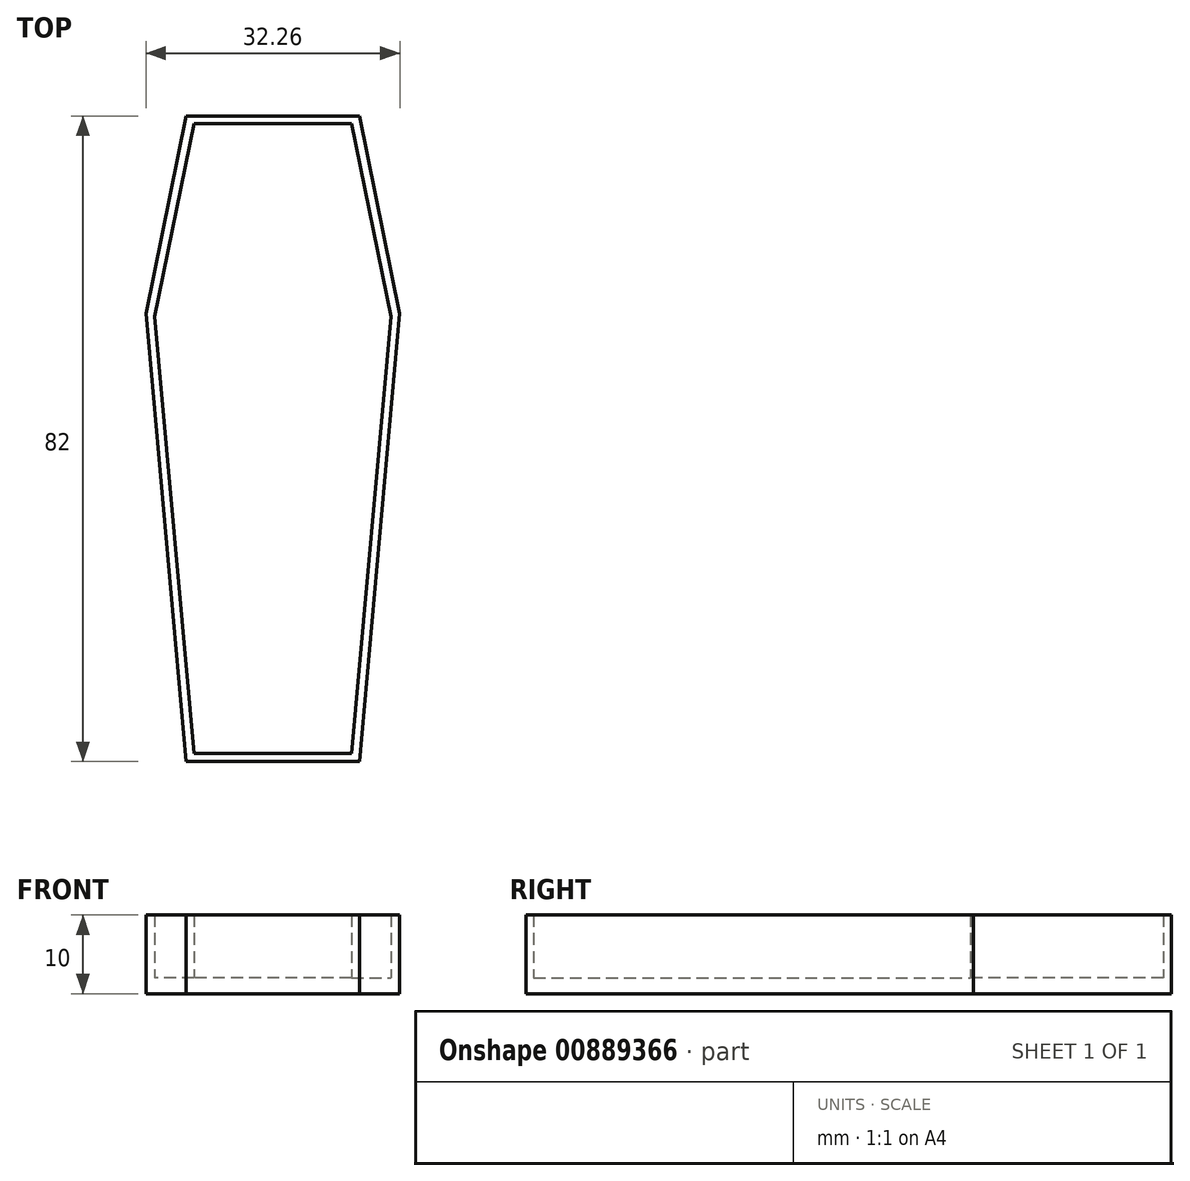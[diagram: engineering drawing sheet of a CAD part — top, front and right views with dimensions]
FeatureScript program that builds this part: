
annotation { "Feature Type Name" : "Feature", "Feature Type Description" : "" }
export const myFeature = defineFeature(function(context is Context, id is Id, definition is map)
    precondition{}
    {
        {
            var Q0;
            Q0=qCreatedBy(makeId("Top.planeOp"),FACE);
            var sketch = newSketch(context, id + "F0", { "sketchPlane" : qUnion([Q0])});
            skLineSegment(sketch, "E0.bottom", {"start": v(10, 40) * mm, "end": v(-10, 40) * mm});
            skLineSegment(sketch, "E0.top", {"start": v(10, -40) * mm, "end": v(-10, -40) * mm});
            skLineSegment(sketch, "E0.left", {"start": v(10, 40) * mm, "end": v(10, -40) * mm});
            skLineSegment(sketch, "E0.right", {"start": v(-10, 40) * mm, "end": v(-10, -40) * mm});
            skPoint(sketch, "E0.middle", {"position": v(0, 0) * mm});
            skLineSegment(sketch, "E1", {"start": v(-10, 40) * mm, "end": v(-15, 15.5) * mm});
            skLineSegment(sketch, "E2", {"start": v(-10, -40) * mm, "end": v(-15, 15.5) * mm});
            skLineSegment(sketch, "E3.MirrorCS", {"start": v(10, -40) * mm, "end": v(15, 15.5) * mm});
            skLineSegment(sketch, "E4.MirrorCS", {"start": v(10, 40) * mm, "end": v(15, 15.5) * mm});
            skLineSegment(sketch, "E5.bottom", {"start": v(-11, 41) * mm, "end": v(11, 41) * mm});
            skLineSegment(sketch, "E5.top", {"start": v(-11, -41) * mm, "end": v(11, -41) * mm});
            skLineSegment(sketch, "E5.left", {"start": v(-11, 41) * mm, "end": v(-11, -41) * mm});
            skLineSegment(sketch, "E5.right", {"start": v(11, 41) * mm, "end": v(11, -41) * mm});
            skLineSegment(sketch, "E6", {"start": v(-11, 41) * mm, "end": v(-16.13, 15.9) * mm});
            skLineSegment(sketch, "E7", {"start": v(-16.13, 15.9) * mm, "end": v(-11, -41) * mm});
            skLineSegment(sketch, "E8.MirrorCS", {"start": v(11, 41) * mm, "end": v(16.13, 15.9) * mm});
            skLineSegment(sketch, "E9.MirrorCS", {"start": v(16.13, 15.9) * mm, "end": v(11, -41) * mm});
            skSolve(sketch);
        }
        {
            var Q0;
            Q0=makeQuery(id+"F0.imprint","IMPRINT",FACE,{"disambiguationData":[TD([[makeQuery(id+"F0.imprint","IMPRINT",EDGE,{"derivedFrom":sQuery(id+"F0.wireOp",EDGE,"E0.bottom")}),1.0]])]});
            var Q1;
            {var subQ0=sQuery(id+"F0.wireOp",EDGE,"E0.right");Q1=makeQuery(id+"F0.imprint","IMPRINT",FACE,{"disambiguationData":[TD([[makeQuery(id+"F0.imprint","IMPRINT",EDGE,{"derivedFrom":subQ0}),-1.0]])]});}
            var Q2;
            {var subQ0=sQuery(id+"F0.wireOp",EDGE,"E0.left");Q2=makeQuery(id+"F0.imprint","IMPRINT",FACE,{"disambiguationData":[TD([[makeQuery(id+"F0.imprint","IMPRINT",EDGE,{"derivedFrom":subQ0}),1.0]])]});}
            var Q3;
            {var subQ0=sQuery(id+"F0.wireOp",EDGE,"E2");var subQ1=sQuery(id+"F0.wireOp",EDGE,"E1");var subQ2=makeQuery(id+"F0.imprint","INTERSECT",VERTEX,{"derivedFrom":[subQ1,subQ0]});Q3=makeQuery(id+"F0.imprint","IMPRINT",FACE,{"disambiguationData":[TD([[makeQuery(id+"F0.imprint","IMPRINT",EDGE,{"disambiguationData":[TD([[subQ2,1.0]])],"derivedFrom":subQ1}),1.0]])]});}
            var Q4;
            {var subQ0=sQuery(id+"F0.wireOp",EDGE,"E4.MirrorCS");var subQ1=sQuery(id+"F0.wireOp",EDGE,"E3.MirrorCS");var subQ2=makeQuery(id+"F0.imprint","INTERSECT",VERTEX,{"derivedFrom":[subQ1,subQ0]});Q4=makeQuery(id+"F0.imprint","IMPRINT",FACE,{"disambiguationData":[TD([[makeQuery(id+"F0.imprint","IMPRINT",EDGE,{"disambiguationData":[TD([[subQ2,1.0]])],"derivedFrom":subQ1}),1.0]])]});}
            extrude(context, id + "F1", {"entities" : qUnion([Q0, Q1, Q2, Q3, Q4]), "depth" : 2 * mm, "offsetDistance" : 25 * mm});
        }
        {
            var Q0;
            {var subQ7=sQuery(id+"F0.wireOp",EDGE,"E6");Q0=makeQuery(id+"F0.imprint","IMPRINT",FACE,{"disambiguationData":[TD([[makeQuery(id+"F0.imprint","IMPRINT",EDGE,{"derivedFrom":subQ7}),1.0]])]});}
            var Q1;
            {var subQ2=sQuery(id+"F0.wireOp",EDGE,"E0.bottom");Q1=makeQuery(id+"F0.imprint","IMPRINT",FACE,{"disambiguationData":[TD([[makeQuery(id+"F0.imprint","IMPRINT",EDGE,{"derivedFrom":subQ2}),-1.0]])]});}
            var Q2;
            {var subQ0=sQuery(id+"F0.wireOp",EDGE,"E8.MirrorCS");Q2=makeQuery(id+"F0.imprint","IMPRINT",FACE,{"disambiguationData":[TD([[makeQuery(id+"F0.imprint","IMPRINT",EDGE,{"derivedFrom":subQ0}),-1.0]])]});}
            var Q3;
            {var subQ2=sQuery(id+"F0.wireOp",EDGE,"E0.top");Q3=makeQuery(id+"F0.imprint","IMPRINT",FACE,{"disambiguationData":[TD([[makeQuery(id+"F0.imprint","IMPRINT",EDGE,{"derivedFrom":subQ2}),1.0]])]});}
            extrude(context, id + "F2", {"entities" : qUnion([Q0, Q1, Q2, Q3]), "operationType" : NewBodyOperationType.ADD, "depth" : 10 * mm, "offsetDistance" : 25 * mm});
        }
    });
